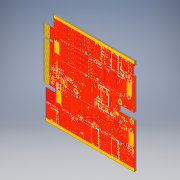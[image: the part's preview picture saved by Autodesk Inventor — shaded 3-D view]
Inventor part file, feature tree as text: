
AUTODESK INVENTOR PART (.ipt)
format: ipt  version: 2018 (Build 220112000, 112)  size: 2,184,704 bytes
history: native  units: in
note: dims shown in document units (in); Inventor stores cm internally (conversion verified against a paired STEP export)
features: sketch x10, other x8, hole x7, extrude x2, chamfer x1, fillet x1, projected_geometry x1
ambient origin geometry x8: Origin, YZ Plane, XZ Plane, XY Plane, X Axis, Y Axis, Z Axis, Center Point
bodies: Solid1 (feature_tree)
feature tree (30):
  extrude  "Extrusion1"  Depth=3.7717in
  chamfer  "Chamfer1"  Distance=0.063in
  fillet  "Fillet1"  Radius=3.7795in
  extrude  "Extrusion5"  Depth=0.0039in
  other  "Decal1"
  other  "Decal2"
  hole  "Hole9"  [1 undecoded]
  hole  "Hole10"  [1 undecoded]
  hole  "Hole11"  [1 undecoded]
  hole  "Hole12"  [1 undecoded]
  hole  "Hole13"  [1 undecoded]
  hole  "Hole14"  [1 undecoded]
  hole  "Hole15"  [1 undecoded]
  other  "BATTERY+"
  other  "VBATT_RBF"
  other  "PGND"
  other  "BATTERY-"
  sketch  "Sketch6"  dims[d0=2.0197in d1=3.7717in]
  projected_geometry  "Projected Loop4"
  sketch  "Sketch14"  dims[d3=0.3937in d4=0.063in d5=0.0in d20=3.7795in]
  sketch  "Sketch15"  dims[d21=3.7795in d22=0.0039in]
  other  "Image5"
  other  "Image6"
  sketch  "Sketch16"  dims[d23=0.0039in d24=0.0787in]
  sketch  "Sketch17"  dims[d25=0.0039in d28=0.4429in]
  sketch  "Sketch18"  dims[d29=2.2047in d31=0.374in]
  sketch  "Sketch19"  dims[d32=1.2008in d34=0.1378in]
  sketch  "Sketch20"  dims[d35=0.4783in d36=1.5413in]
  sketch  "Sketch21"  dims[d37=0.5709in d38=0.0453in]
  sketch  "Sketch22"  dims[d39=0.0709in d40=2.7559in d42=0.0709in d43=1.9685in d45=0.0709in d48=0.0787in d49=0.1339in d50=0.0748in d51=0.3307in d52=0.9449in d53=0.0197in d54=0.0787in d55=45.0deg d56=0.0197in d69=0.2362in d70=0.0394in d71=0.6102in d77=0.3937in d78=0.0in d81=0.0787in d82=1.378in d83=0.315in d151=0.1181in d152=0.2362in d153=0.1575in d154=0.0787in d155=90.0deg d156=0.315in d157=0.8108in d158=0.0866in d159=0.2362in d160=0.1575in d161=0.0787in d162=90.0deg d163=0.315in d164=0.8108in d165=0.0591in d166=0.2362in d167=0.1575in d168=0.0787in d169=90.0deg d170=0.315in d171=0.8108in d172=0.0472in d173=0.2362in d174=0.1575in d175=0.0787in d176=90.0deg d177=0.315in d178=0.8108in d179=0.0276in d180=0.2362in d181=0.1575in d182=0.0787in d183=90.0deg d184=0.315in d185=0.8108in d186=0.0138in d187=0.2362in d188=0.1575in d189=0.0787in d190=90.0deg d191=0.315in d192=0.8108in d193=0.0118in d194=0.2362in d195=0.1575in d196=0.0787in d197=90.0deg d198=0.315in d199=0.8108in]
note: 7 required parameter values undecoded (feature->parameter linkage not recoverable at this tier; creation-order binding heuristic only, values carry confidence <= 0.55)
